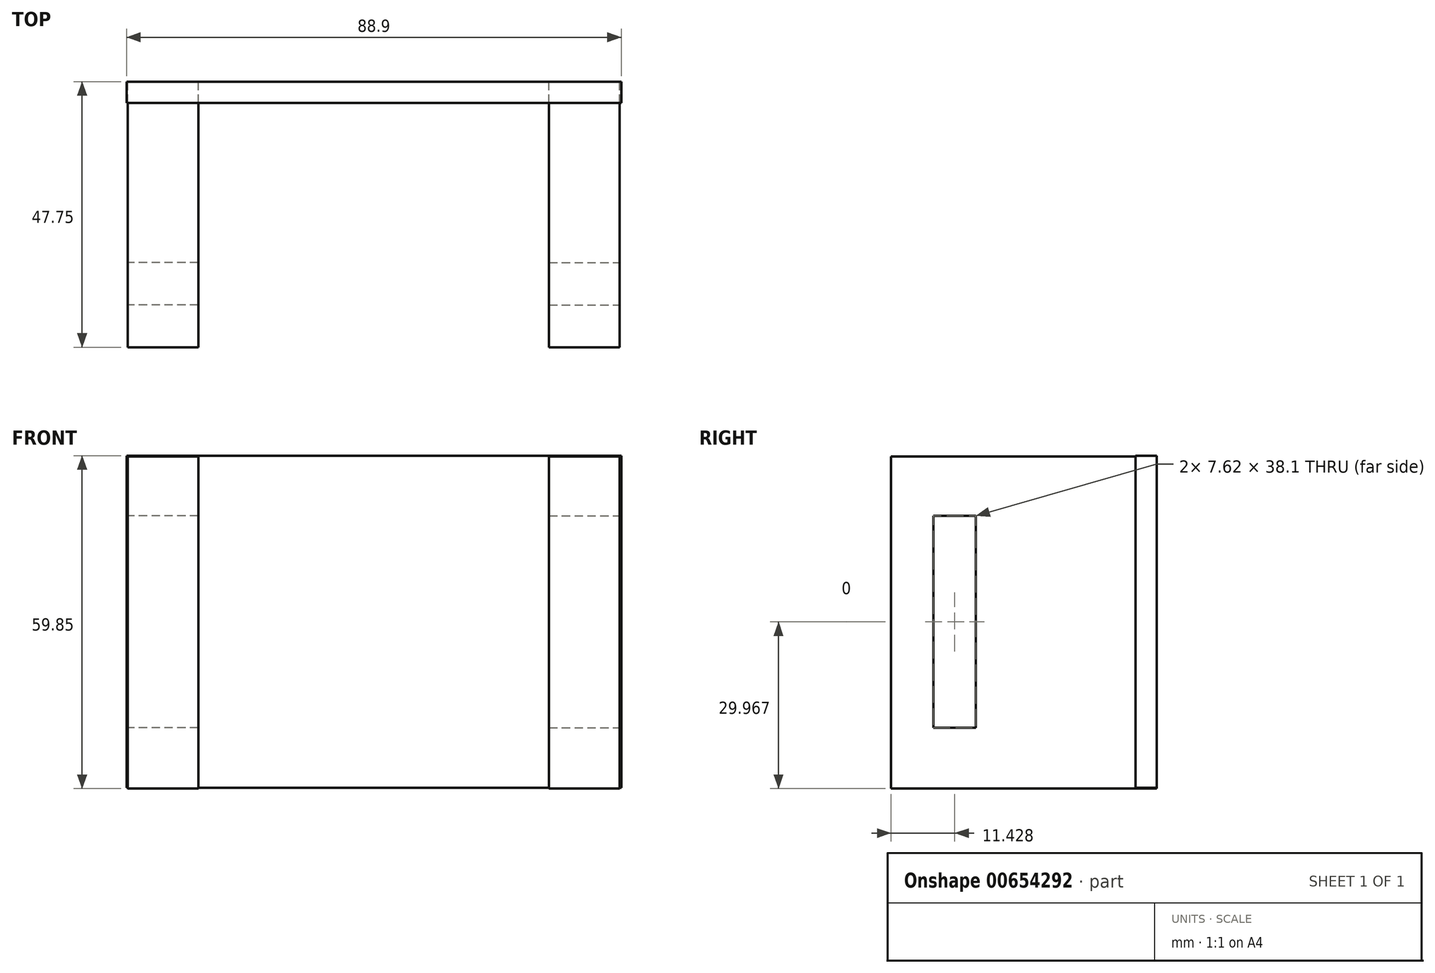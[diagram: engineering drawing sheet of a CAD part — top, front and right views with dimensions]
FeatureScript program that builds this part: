
annotation { "Feature Type Name" : "Feature", "Feature Type Description" : "" }
export const myFeature = defineFeature(function(context is Context, id is Id, definition is map)
    precondition{}
    {
        {
            var Q0;
            Q0=qCreatedBy(makeId("Front.planeOp"),FACE);
            var sketch = newSketch(context, id + "F0", { "sketchPlane" : qUnion([Q0])});
            skLineSegment(sketch, "E0.bottom", {"start": v(-44.76, 23.59) * mm, "end": v(44.14, 23.59) * mm});
            skLineSegment(sketch, "E0.top", {"start": v(-44.76, -36.1) * mm, "end": v(44.14, -36.1) * mm});
            skLineSegment(sketch, "E0.left", {"start": v(-44.76, 23.59) * mm, "end": v(-44.76, -36.1) * mm});
            skLineSegment(sketch, "E0.right", {"start": v(44.14, 23.59) * mm, "end": v(44.14, -36.1) * mm});
            skSolve(sketch);
        }
        {
            var Q0;
            Q0 = qSketchRegion(id + "F0", true);
            extrude(context, id + "F1", {"entities" : qUnion([Q0]), "depth" : 3.8 * mm, "offsetDistance" : 25.4 * mm});
        }
        {
            var Q0;
            Q0=qCreatedBy(makeId("Front.planeOp"),FACE);
            var sketch = newSketch(context, id + "F2", { "sketchPlane" : qUnion([Q0])});
            skLineSegment(sketch, "E1.bottom", {"start": v(139.14, 87.41) * mm, "end": v(109.14, 87.41) * mm});
            skLineSegment(sketch, "E1.left", {"start": v(139.14, 87.41) * mm, "end": v(139.14, -17.39) * mm});
            skLineSegment(sketch, "E2.bottom", {"start": v(-44.56, 23.43) * mm, "end": v(-31.86, 23.43) * mm});
            skLineSegment(sketch, "E2.top", {"start": v(-44.56, -36.26) * mm, "end": v(-31.86, -36.26) * mm});
            skLineSegment(sketch, "E2.left", {"start": v(-44.56, 23.43) * mm, "end": v(-44.56, -36.26) * mm});
            skLineSegment(sketch, "E2.right", {"start": v(-31.86, 23.43) * mm, "end": v(-31.86, -36.26) * mm});
            skLineSegment(sketch, "E3.bottom", {"start": v(43.84, 23.43) * mm, "end": v(31.14, 23.43) * mm});
            skLineSegment(sketch, "E3.top", {"start": v(43.84, -36.26) * mm, "end": v(31.14, -36.26) * mm});
            skLineSegment(sketch, "E3.left", {"start": v(43.84, 23.43) * mm, "end": v(43.84, -36.26) * mm});
            skLineSegment(sketch, "E3.right", {"start": v(31.14, 23.43) * mm, "end": v(31.14, -36.26) * mm});
            skSolve(sketch);
        }
        {
            var Q0;
            Q0 = qSketchRegion(id + "F2", true);
            extrude(context, id + "F3", {"entities" : qUnion([Q0]), "operationType" : NewBodyOperationType.ADD, "depth" : 47.75 * mm, "offsetDistance" : 25.4 * mm});
        }
        {
            var Q0;
            Q0=makeQuery(id+"F3.opExtrude","SWEPT_FACE",FACE,{"disambiguationData":[OSD([sQuery(id+"F2.wireOp",EDGE,"E3.left")])]});
            var sketch = newSketch(context, id + "F4", { "sketchPlane" : qUnion([Q0])});
            skLineSegment(sketch, "E4.bottom", {"start": v(-40.13, 12.76) * mm, "end": v(-32.51, 12.76) * mm});
            skLineSegment(sketch, "E4.top", {"start": v(-40.13, -25.34) * mm, "end": v(-32.51, -25.34) * mm});
            skLineSegment(sketch, "E4.left", {"start": v(-40.13, 12.76) * mm, "end": v(-40.13, -25.34) * mm});
            skLineSegment(sketch, "E4.right", {"start": v(-32.51, 12.76) * mm, "end": v(-32.51, -25.34) * mm});
            skSolve(sketch);
        }
        {
            var Q0;
            Q0=makeQuery(id+"F4.imprint","IMPRINT",FACE,{"disambiguationData":[TD([[makeQuery(id+"F4.imprint","IMPRINT",EDGE,{"derivedFrom":sQuery(id+"F4.wireOp",EDGE,"E4.bottom")}),-1.0]])]});
            extrude(context, id + "F5", {"entities" : qUnion([Q0]), "operationType" : NewBodyOperationType.REMOVE, "oppositeDirection" : true, "depth" : 25.4 * mm, "offsetDistance" : 25.4 * mm, "hasSecondDirection" : true, "secondDirectionOppositeDirection" : false, "secondDirectionDepth" : 25.4 * mm});
        }
        {
            var Q0;
            Q0=makeQuery(id+"F3.opExtrude","SWEPT_FACE",FACE,{"disambiguationData":[OSD([sQuery(id+"F2.wireOp",EDGE,"E2.left")])]});
            var sketch = newSketch(context, id + "F6", { "sketchPlane" : qUnion([Q0])});
            skLineSegment(sketch, "E5.bottom", {"start": v(40.13, 12.76) * mm, "end": v(32.51, 12.76) * mm});
            skLineSegment(sketch, "E5.top", {"start": v(40.13, -25.34) * mm, "end": v(32.51, -25.34) * mm});
            skLineSegment(sketch, "E5.left", {"start": v(40.13, 12.76) * mm, "end": v(40.13, -25.34) * mm});
            skLineSegment(sketch, "E5.right", {"start": v(32.51, 12.76) * mm, "end": v(32.51, -25.34) * mm});
            skSolve(sketch);
        }
        {
            var Q0;
            Q0=makeQuery(id+"F6.imprint","IMPRINT",FACE,{"disambiguationData":[TD([[makeQuery(id+"F6.imprint","IMPRINT",EDGE,{"derivedFrom":sQuery(id+"F6.wireOp",EDGE,"E5.bottom")}),1.0]])]});
            extrude(context, id + "F7", {"entities" : qUnion([Q0]), "operationType" : NewBodyOperationType.REMOVE, "oppositeDirection" : true, "depth" : 25.4 * mm, "offsetDistance" : 25.4 * mm, "hasSecondDirection" : true, "secondDirectionOppositeDirection" : false, "secondDirectionDepth" : 25.4 * mm});
        }
    });
